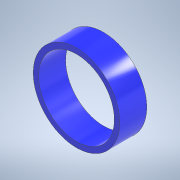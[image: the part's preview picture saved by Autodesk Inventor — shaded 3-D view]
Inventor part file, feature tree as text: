
AUTODESK INVENTOR PART (.ipt)
format: ipt  version: 2022 (Build 260153000, 153)  size: 108,032 bytes
history: imported  units: in
note: dims shown in document units (in); Inventor stores cm internally (conversion verified against a paired STEP export)
features: imported_body x1
ambient origin geometry x8: Origin, YZ Plane, XZ Plane, XY Plane, X Axis, Y Axis, Z Axis, Center Point
bodies: Solid1 (imported_parasolid), Body1 (imported_parasolid)
feature tree (1):
  imported_body  NMx_Import_Brep_tag  [imported B-rep: ~4 faces, bbox_mm=[1.0, 0.0, 5.0]]
